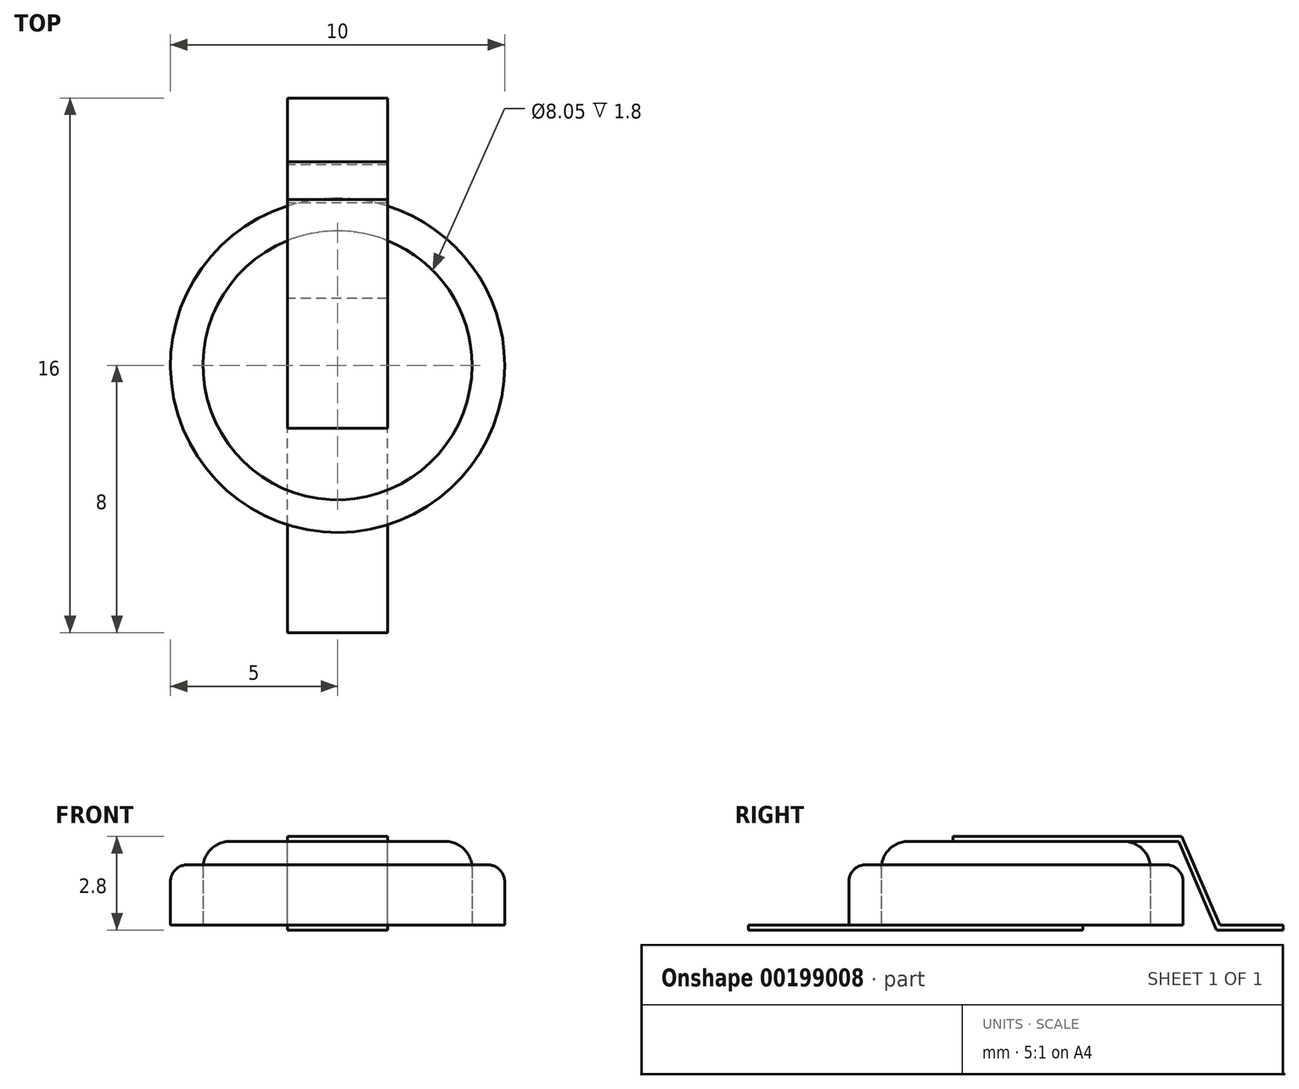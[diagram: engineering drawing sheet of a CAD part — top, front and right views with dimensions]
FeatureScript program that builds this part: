
annotation { "Feature Type Name" : "Feature", "Feature Type Description" : "" }
export const myFeature = defineFeature(function(context is Context, id is Id, definition is map)
    precondition{}
    {
        {
            var Q0;
            Q0=qCreatedBy(makeId("Top.planeOp"),FACE);
            var sketch = newSketch(context, id + "F0", { "sketchPlane" : qUnion([Q0])});
            skCircle(sketch, "E0", {"center": v(0, 0) * mm, "radius": 5 * mm});
            skCircle(sketch, "E1", {"center": v(0, 0) * mm, "radius": 4.03 * mm});
            skSolve(sketch);
        }
        {
            var Q0;
            Q0=makeQuery(id+"F0.imprint","IMPRINT",FACE,{"disambiguationData":[TD([[makeQuery(id+"F0.imprint","IMPRINT",EDGE,{"derivedFrom":sQuery(id+"F0.wireOp",EDGE,"E1")}),1.0]])]});
            extrude(context, id + "F1", {"entities" : qUnion([Q0]), "depth" : 2.5 * mm});
        }
        {
            var Q0;
            Q0=makeQuery(id+"F0.imprint","IMPRINT",FACE,{"disambiguationData":[TD([[makeQuery(id+"F0.imprint","IMPRINT",EDGE,{"derivedFrom":sQuery(id+"F0.wireOp",EDGE,"E0")}),1.0]])]});
            var Q1;
            Q1=sQuery(id+"F0.wireOp",EDGE,"E0");
            extrude(context, id + "F2", {"entities" : qUnion([Q0]), "surfaceEntities" : qUnion([Q1]), "depth" : 1.8 * mm});
        }
        {
            var Q0;
            Q0=qCreatedBy(makeId("Right.planeOp"),FACE);
            var sketch = newSketch(context, id + "F3", { "sketchPlane" : qUnion([Q0])});
            skLineSegment(sketch, "E2", {"start": v(0, 0) * mm, "end": v(0, 2.5) * mm});
            skLineSegment(sketch, "E3", {"start": v(0, 2.5) * mm, "end": v(8, 2.5) * mm});
            skLineSegment(sketch, "E4", {"start": v(0, 2.5) * mm, "end": v(-5, 2.5) * mm});
            skLineSegment(sketch, "E5", {"start": v(8, 2.5) * mm, "end": v(8, 0) * mm});
            skLineSegment(sketch, "E6", {"start": v(8, 0) * mm, "end": v(-8, 0) * mm});
            skLineSegment(sketch, "E7", {"start": v(4.87, 2.5) * mm, "end": v(-1.88, 2.5) * mm});
            skLineSegment(sketch, "E8", {"start": v(8, 0) * mm, "end": v(8, -0.15) * mm});
            skLineSegment(sketch, "E9", {"start": v(8, -0.15) * mm, "end": v(6, -0.15) * mm});
            skLineSegment(sketch, "E10", {"start": v(6, -0.15) * mm, "end": v(4.87, 2.5) * mm});
            skLineSegment(sketch, "E11.0", {"start": v(4.97, 2.65) * mm, "end": v(-1.88, 2.65) * mm});
            skLineSegment(sketch, "E11.1", {"start": v(6.1, 0) * mm, "end": v(4.97, 2.65) * mm});
            skLineSegment(sketch, "E11.2", {"start": v(8, 0) * mm, "end": v(6.1, 0) * mm});
            skLineSegment(sketch, "E12.bottom", {"start": v(-8, 0) * mm, "end": v(2, 0) * mm});
            skLineSegment(sketch, "E12.top", {"start": v(-8, -0.15) * mm, "end": v(2, -0.15) * mm});
            skLineSegment(sketch, "E12.left", {"start": v(-8, 0) * mm, "end": v(-8, -0.15) * mm});
            skLineSegment(sketch, "E12.right", {"start": v(2, 0) * mm, "end": v(2, -0.15) * mm});
            skLineSegment(sketch, "E13", {"start": v(-1.88, 2.65) * mm, "end": v(-1.88, 2.5) * mm});
            skSolve(sketch);
        }
        {
            var Q0;
            {var subQ5=sQuery(id+"F3.wireOp",EDGE,"E11.0");Q0=makeQuery(id+"F3.imprint","IMPRINT",FACE,{"disambiguationData":[TD([[makeQuery(id+"F3.imprint","IMPRINT",EDGE,{"derivedFrom":subQ5}),1.0]])]});}
            var Q1;
            {var subQ1=sQuery(id+"F3.wireOp",EDGE,"E3");var subQ3=sQuery(id+"F3.wireOp",EDGE,"E11.1");var subQ4=makeQuery(id+"F3.imprint","INTERSECT",VERTEX,{"derivedFrom":[subQ1,subQ3]});Q1=makeQuery(id+"F3.imprint","IMPRINT",FACE,{"disambiguationData":[TD([[makeQuery(id+"F3.imprint","IMPRINT",EDGE,{"disambiguationData":[TD([[subQ4,1.0]])],"derivedFrom":subQ1}),-1.0]])]});}
            var Q2;
            Q2=makeQuery(id+"F3.imprint","IMPRINT",FACE,{"disambiguationData":[TD([[makeQuery(id+"F3.imprint","IMPRINT",EDGE,{"derivedFrom":sQuery(id+"F3.wireOp",EDGE,"E8")}),-1.0]])]});
            var Q3;
            Q3=makeQuery(id+"F3.imprint","IMPRINT",FACE,{"disambiguationData":[TD([[makeQuery(id+"F3.imprint","IMPRINT",EDGE,{"derivedFrom":sQuery(id+"F3.wireOp",EDGE,"E12.top")}),1.0]])]});
            extrude(context, id + "F4", {"entities" : qUnion([Q0, Q1, Q2, Q3]), "depth" : 3 * mm, "symmetric" : true});
        }
        {
            var Q0;
            Q0=makeQuery(id+"F1.opExtrude","CAP_EDGE",EDGE,{"disambiguationData":[OSD([sQuery(id+"F0.wireOp",EDGE,"E1")])],"isStart":false});
            fillet(context, id + "F5", {"entities" : qUnion([Q0]), "radius" : 0.8 * mm, "tangentPropagation" : true, "allowEdgeOverflow" : false});
        }
        {
            var Q0;
            Q0=makeQuery(id+"F2.opExtrude","CAP_EDGE",EDGE,{"disambiguationData":[OSD([sQuery(id+"F0.wireOp",EDGE,"E0")])],"isStart":false});
            fillet(context, id + "F6", {"entities" : qUnion([Q0]), "radius" : 0.5 * mm, "tangentPropagation" : true, "allowEdgeOverflow" : false});
        }
    });
